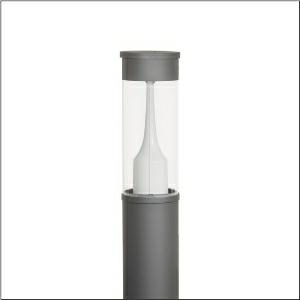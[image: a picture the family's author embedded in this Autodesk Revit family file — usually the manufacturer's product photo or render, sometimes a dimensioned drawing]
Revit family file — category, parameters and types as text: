
# Revit family: city-light_260_iq___st1_2a_5xa5295mf14h_84f0
name_source: partatom
category: Lighting Fixtures
units: mm (PartAtom-declared; Revit-internal decimal feet)

## family parameters
Cut with Voids When Loaded = No
Host = Face
Light Source = No
Part Type = Normal
Room Calculation Point = No
Round Connector Dimension = Use Diameter
Shared = No

## types (1)
- --- (1 x LED, 1540 lm, 11.8 W, 2700K)
    Apparent Load = 12 VA
    CIE Flux Codes = 22 61 93 96 100
    Color Rendering = 70
    Color Temperature = 2700K
    Default Elevation = 1800 mm
    Description = City-Light 260 iQ, light pillar, Module 540 iQ-SR, primary light control with 3 zone facetted reflector, of plastic, silver coated, highly specular, structured, primary optical cover: cover, of PMMA, transparent, partly coated, light distribution: ST1.2a, primary light characteristic: asymmetric, LED, High Power LED, rated luminous flux: 1.540lm, luminous efficacy: 131lm/W, light colour: 727, colour temperature: 2700K, control gear: iQ Street-Remote, control: pre-setting: logarithmic dimming characteristic, Street-Remote, Auto-Match, Temp-Guard, Lumen-Switch, Night-Set, Smart-Wire, Light-Fading, Desk-Remote (wireless, voltage-free reading and setting of iQ features in the workshop via application-optimized NFC function/RFID function), optimised constant luminous flux control (CLO 2.0), with terminal, 6-pole, max. 2.5mm², mains connection: 230..240V, AC, 50/60Hz, start of lifetime: 12W, end of service life: 12W, reduction: 6W, luminaire housing, cylindrical, of extruded aluminium section, coated, Siteco® metallic grey (DB 702S), length: 2.600mm, diameter: 200mm, Module 540 iQ-SR, traffic white (RAL 9016), equipment: standard, protection rating (complete): IP65, insulation class (complete): insulation class II (safety insulation), certification: CE, ENEC, VDE, packaging unit: 1 piece

Light Distribution: ST1.2a
    Height = 500 mm
    Lamp = 1 x LED
    Lamp Light Flux = 1540 lm
    Lamp Power = 11.8 W
    Lamp count = 1
    Length = 200 mm  [stored 0.656168 ft]
    Luminous efficacy = 131 lm/W
    Manufacturer = Siteco
    ModVariant = No
    Model = 5XA5295MF14H
    Mounting Place = Floor
    Mounting Type = Freestanding
    Number of Poles = 1
    OnlyDefault = Yes
    Power Factor = 1
    Product Name = City-Light 260 iQ | ST1.2a
    Product group = light pillar
    ProductGroupID = 1301
    Protection Class = Protection class II
    Protection Degree = IP 65
    RLX_Detail_Level = 1
    RLX_Emergency_Light_Flux = 0 lm
    RLX_Emergency_Type = 0
    RLX_Emergency_Type_DB = No
    RlxData = <blob elided: 60713 chars, md5=fb46bb1b>
    Socket = socket
    Standby Power = 0 W
    System Light Flux = 1540 lm
    System Power = 12 W
    Type Comments = factory setting: luminous flux: 100 % | dim-lin: 254 | 472 mA
    Type Image = l_1006918.jpg
    URL = http://relux.com
    VarID = @adj_152579
    Voltage = 0 V
    Weight = 0.00 kg
    Width = 0 mm  [stored 0 ft]

note: [stored X ft] marks values corroborated as IEEE doubles in the binary element streams (Revit-internal decimal feet)

## geometry (parser evidence)
native form markers: Blend x4, Sweep x12
no freeform markers — native parametric forms only
